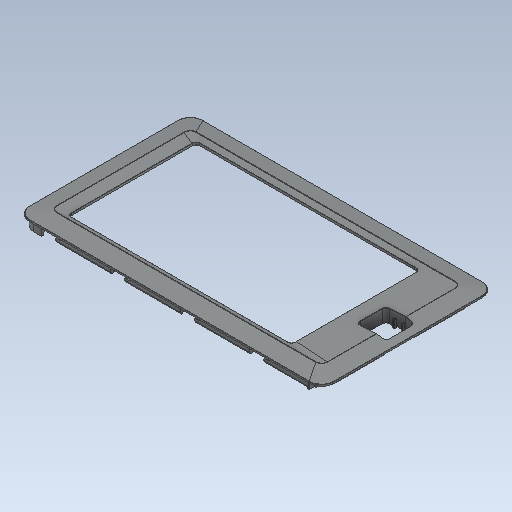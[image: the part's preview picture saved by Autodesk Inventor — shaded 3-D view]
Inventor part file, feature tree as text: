
AUTODESK INVENTOR PART (.ipt)
format: ipt  version: 2020 (Build 240168000, 168)  size: 2,560,000 bytes
history: native  units: in
note: dims shown in document units (in); Inventor stores cm internally (conversion verified against a paired STEP export)
features: fillet x1
ambient origin geometry x8: Origin, YZ Plane, XZ Plane, XY Plane, X Axis, Y Axis, Z Axis, Center Point
bodies: Solid1 (feature_tree)
feature tree (1):
  fillet  "Fillet44"  [1 undecoded]
note: 1 required parameter value undecoded (feature->parameter linkage not recoverable at this tier; creation-order binding heuristic only, values carry confidence <= 0.55)
